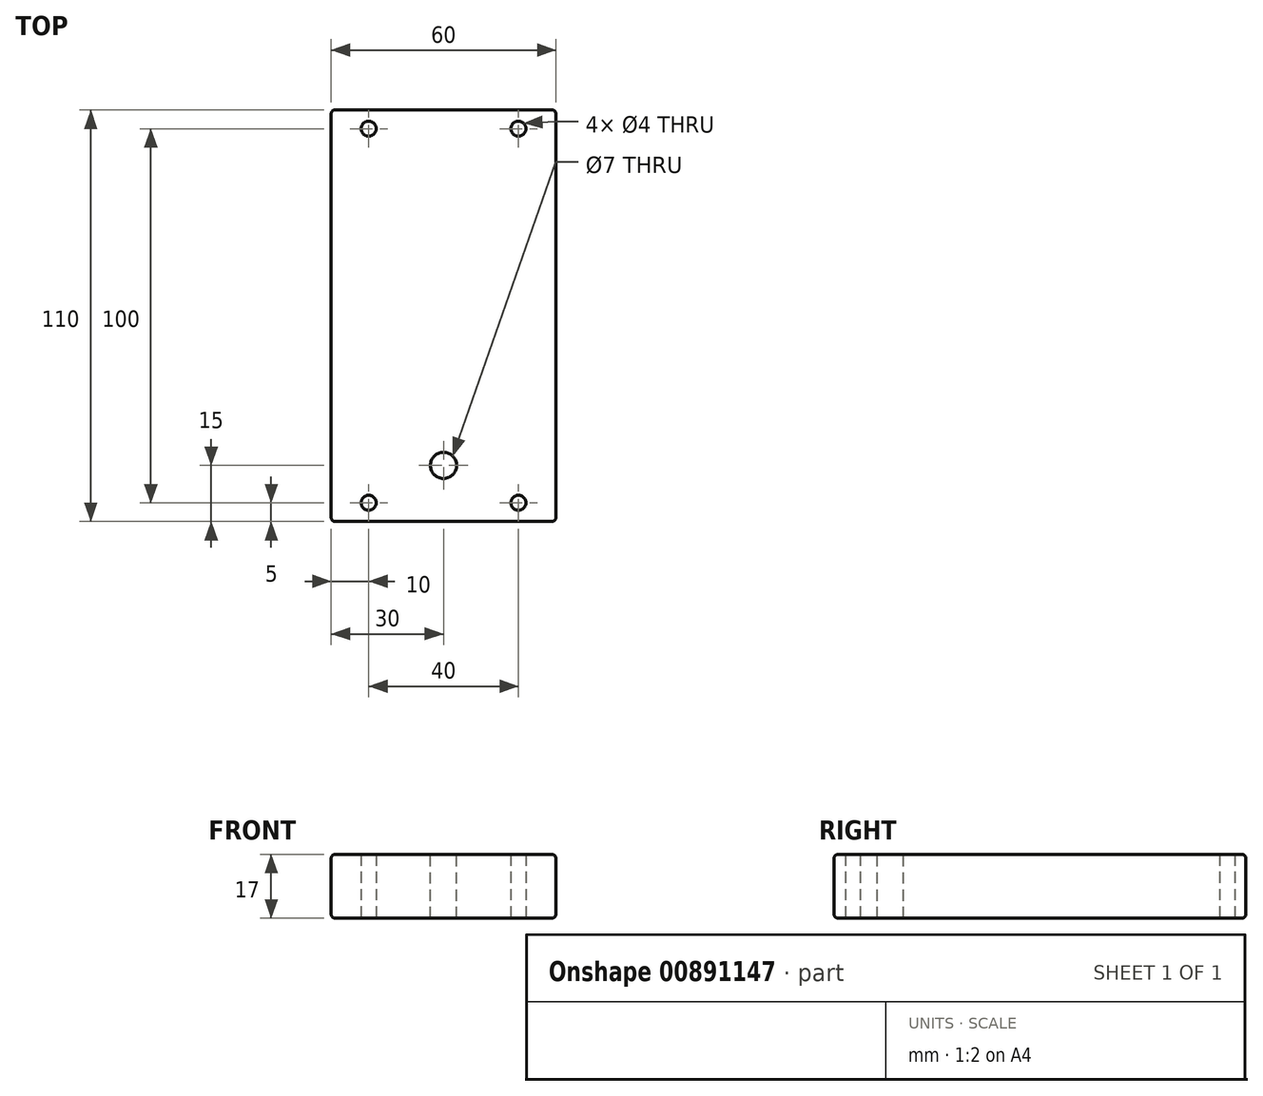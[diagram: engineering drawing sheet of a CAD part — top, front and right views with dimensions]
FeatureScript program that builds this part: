
annotation { "Feature Type Name" : "Feature", "Feature Type Description" : "" }
export const myFeature = defineFeature(function(context is Context, id is Id, definition is map)
    precondition{}
    {
        {
            var Q0;
            Q0=qCreatedBy(makeId("Top.planeOp"),FACE);
            var sketch = newSketch(context, id + "F0", { "sketchPlane" : qUnion([Q0])});
            skLineSegment(sketch, "E0.bottom", {"start": v(-30, -55) * mm, "end": v(30, -55) * mm});
            skLineSegment(sketch, "E0.top", {"start": v(-30, 55) * mm, "end": v(30, 55) * mm});
            skLineSegment(sketch, "E0.left", {"start": v(-30, -55) * mm, "end": v(-30, 55) * mm});
            skLineSegment(sketch, "E0.right", {"start": v(30, -55) * mm, "end": v(30, 55) * mm});
            skPoint(sketch, "E0.middle", {"position": v(0, 0) * mm});
            skCircle(sketch, "E1", {"center": v(-20, 50) * mm, "radius": 2 * mm});
            skLineSegment(sketch, "E2", {"start": v(0, 72.46) * mm, "end": v(0, -69.58) * mm, "construction": true});
            skLineSegment(sketch, "E3", {"start": v(-47.96, 0) * mm, "end": v(80.82, 0) * mm, "construction": true});
            skCircle(sketch, "E4.MirrorC", {"center": v(20, 50) * mm, "radius": 2 * mm});
            skCircle(sketch, "E5.MirrorC", {"center": v(-20, -50) * mm, "radius": 2 * mm});
            skCircle(sketch, "E6.MirrorC", {"center": v(20, -50) * mm, "radius": 2 * mm});
            skSolve(sketch);
        }
        {
            var Q0;
            Q0 = qSketchRegion(id + "F0", true);
            extrude(context, id + "F1", {"entities" : qUnion([Q0]), "endBound" : BoundingType.SYMMETRIC, "depth" : 17 * mm, "offsetDistance" : 25 * mm});
        }
        {
            var Q0;
            Q0=makeQuery(id+"F1.opExtrude","CAP_EDGE",EDGE,{"disambiguationData":[OSD([sQuery(id+"F0.wireOp",EDGE,"E0.right")])],"isStart":false});
            var Q1;
            Q1=makeQuery(id+"F1.opExtrude","CAP_EDGE",EDGE,{"disambiguationData":[OSD([sQuery(id+"F0.wireOp",EDGE,"E0.bottom")])],"isStart":false});
            var Q2;
            Q2=makeQuery(id+"F1.opExtrude","CAP_EDGE",EDGE,{"disambiguationData":[OSD([sQuery(id+"F0.wireOp",EDGE,"E0.left")])],"isStart":false});
            var Q3;
            Q3=makeQuery(id+"F1.opExtrude","CAP_EDGE",EDGE,{"disambiguationData":[OSD([sQuery(id+"F0.wireOp",EDGE,"E0.top")])],"isStart":false});
            var Q4;
            Q4=makeQuery(id+"F1.opExtrude","CAP_EDGE",EDGE,{"disambiguationData":[OSD([sQuery(id+"F0.wireOp",EDGE,"E0.right")])],"isStart":true});
            var Q5;
            Q5=makeQuery(id+"F1.opExtrude","SWEPT_EDGE",EDGE,{"disambiguationData":[OSD([sQuery(id+"F0.wireOp",EDGE,"E0.bottom"),sQuery(id+"F0.wireOp",EDGE,"E0.right")])]});
            var Q6;
            Q6=makeQuery(id+"F1.opExtrude","SWEPT_EDGE",EDGE,{"disambiguationData":[OSD([sQuery(id+"F0.wireOp",EDGE,"E0.top"),sQuery(id+"F0.wireOp",EDGE,"E0.right")])]});
            var Q7;
            Q7=makeQuery(id+"F1.opExtrude","CAP_EDGE",EDGE,{"disambiguationData":[OSD([sQuery(id+"F0.wireOp",EDGE,"E0.top")])],"isStart":true});
            var Q8;
            Q8=makeQuery(id+"F1.opExtrude","CAP_EDGE",EDGE,{"disambiguationData":[OSD([sQuery(id+"F0.wireOp",EDGE,"E0.left")])],"isStart":true});
            var Q9;
            Q9=makeQuery(id+"F1.opExtrude","SWEPT_EDGE",EDGE,{"disambiguationData":[OSD([sQuery(id+"F0.wireOp",EDGE,"E0.top"),sQuery(id+"F0.wireOp",EDGE,"E0.left")])]});
            var Q10;
            Q10=makeQuery(id+"F1.opExtrude","SWEPT_EDGE",EDGE,{"disambiguationData":[OSD([sQuery(id+"F0.wireOp",EDGE,"E0.bottom"),sQuery(id+"F0.wireOp",EDGE,"E0.left")])]});
            var Q11;
            Q11=makeQuery(id+"F1.opExtrude","CAP_EDGE",EDGE,{"disambiguationData":[OSD([sQuery(id+"F0.wireOp",EDGE,"E0.bottom")])],"isStart":true});
            fillet(context, id + "F2", {"entities" : qUnion([Q0, Q1, Q2, Q3, Q4, Q5, Q6, Q7, Q8, Q9, Q10, Q11]), "radius" : 1 * mm, "tangentPropagation" : true, "allowEdgeOverflow" : false});
        }
        {
            var Q0;
            Q0=makeQuery(id+"F1.opExtrude","CAP_FACE",FACE,{"disambiguationData":[OSD([sQuery(id+"F0.wireOp",EDGE,"E0.bottom"),sQuery(id+"F0.wireOp",EDGE,"E0.top"),sQuery(id+"F0.wireOp",EDGE,"E0.left"),sQuery(id+"F0.wireOp",EDGE,"E0.right"),sQuery(id+"F0.wireOp",EDGE,"E1"),sQuery(id+"F0.wireOp",EDGE,"E4.MirrorC"),sQuery(id+"F0.wireOp",EDGE,"E5.MirrorC"),sQuery(id+"F0.wireOp",EDGE,"E6.MirrorC")])],"isStart":false});
            var sketch = newSketch(context, id + "F3", { "sketchPlane" : qUnion([Q0])});
            skLineSegment(sketch, "E7", {"start": v(0, 0) * mm, "end": v(-11.46, 0) * mm, "construction": true});
            skCircle(sketch, "E8.MirrorC", {"center": v(0, -40) * mm, "radius": 3.5 * mm});
            skPoint(sketch, "E9.center.orphan", {"position": v(0, 40) * mm});
            skSolve(sketch);
        }
        {
            var Q0;
            Q0 = qSketchRegion(id + "F3", true);
            extrude(context, id + "F4", {"entities" : qUnion([Q0]), "operationType" : NewBodyOperationType.REMOVE, "oppositeDirection" : true, "depth" : 25 * mm, "offsetDistance" : 25 * mm});
        }
    });
